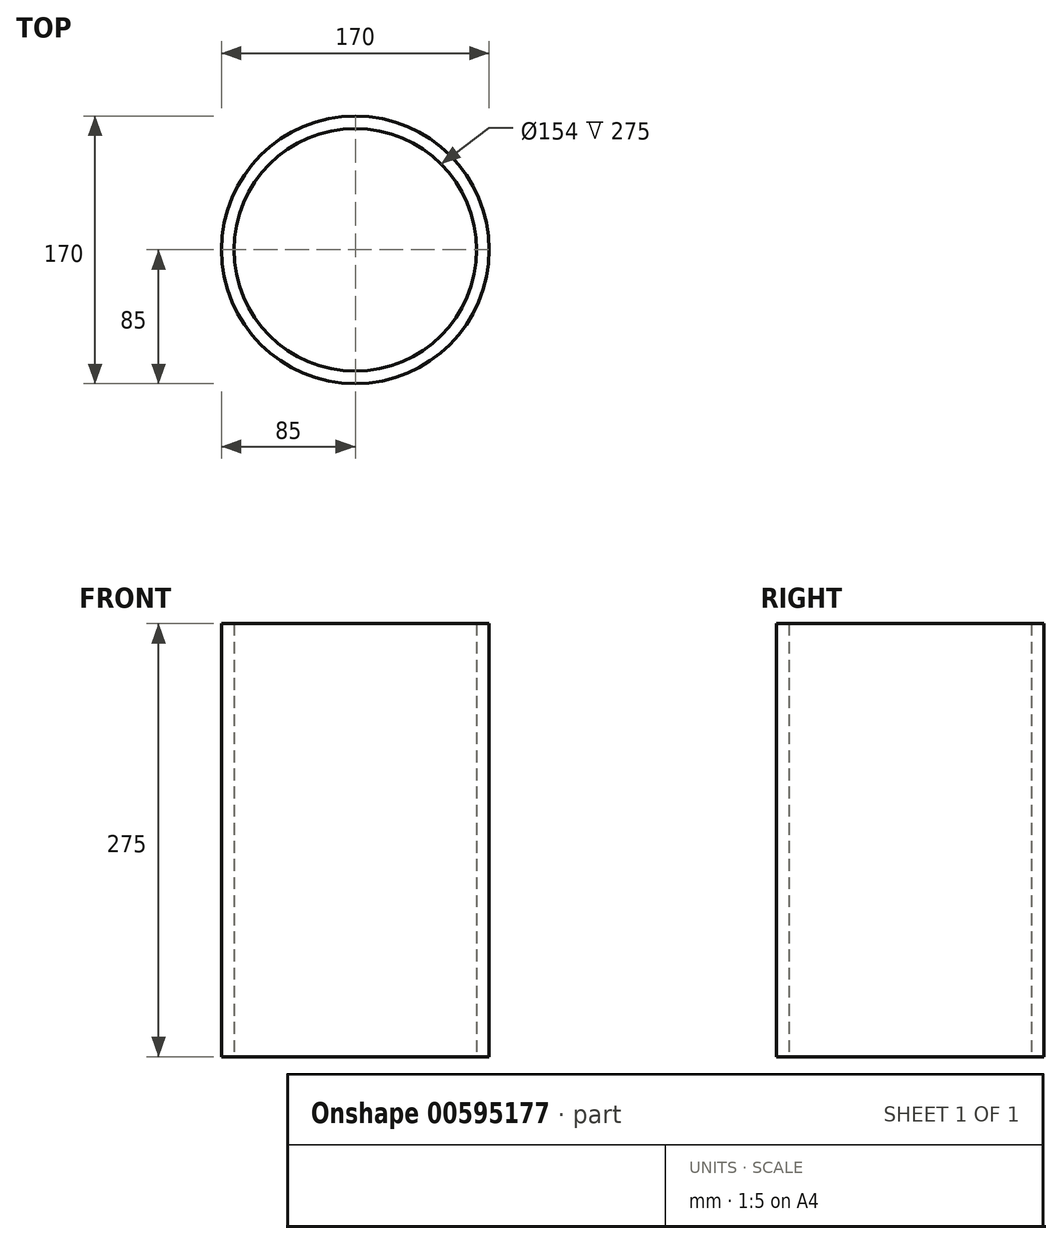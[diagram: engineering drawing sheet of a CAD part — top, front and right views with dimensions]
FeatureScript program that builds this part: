
annotation { "Feature Type Name" : "Feature", "Feature Type Description" : "" }
export const myFeature = defineFeature(function(context is Context, id is Id, definition is map)
    precondition{}
    {
        {
            var Q0;
            Q0=qCreatedBy(makeId("Top.planeOp"),FACE);
            var sketch = newSketch(context, id + "F0", { "sketchPlane" : qUnion([Q0])});
            skCircle(sketch, "E0", {"center": v(0, 0) * mm, "radius": 85 * mm});
            skCircle(sketch, "E1.0", {"center": v(0, 0) * mm, "radius": 77 * mm});
            skSolve(sketch);
        }
        {
            var Q0;
            Q0=makeQuery(id+"F0.imprint","IMPRINT",FACE,{"disambiguationData":[TD([[makeQuery(id+"F0.imprint","IMPRINT",EDGE,{"derivedFrom":sQuery(id+"F0.wireOp",EDGE,"E0")}),1.0]])]});
            extrude(context, id + "F1", {"entities" : qUnion([Q0]), "depth" : 315 * mm, "offsetDistance" : 25 * mm});
        }
        {
            var Q0;
            Q0=qCreatedBy(makeId("Front.planeOp"),FACE);
            cPlane(context, id + "F2", {"entities" : qUnion([Q0]), "cplaneType" : CPlaneType.OFFSET, "offset" : 85 * mm, "oppositeDirection" : true, "width" : 150 * mm, "height" : 150 * mm});
        }
        {
            var Q0;
            Q0=makeQuery(id+"F1.opExtrude","CAP_FACE",FACE,{"disambiguationData":[OSD([sQuery(id+"F0.wireOp",EDGE,"E0"),sQuery(id+"F0.wireOp",EDGE,"E1.0")])],"isStart":false});
            var sketch = newSketch(context, id + "F3", { "sketchPlane" : qUnion([Q0])});
            skCircle(sketch, "E2", {"center": v(0, 0) * mm, "radius": 90 * mm});
            skSolve(sketch);
        }
        {
            var Q0;
            Q0=makeQuery(id+"F3.imprint","IMPRINT",FACE,{"disambiguationData":[TD([[makeQuery(id+"F3.imprint","IMPRINT",EDGE,{"derivedFrom":makeQuery(id+"F1.opExtrude","CAP_EDGE",EDGE,{"disambiguationData":[OSD([sQuery(id+"F0.wireOp",EDGE,"E1.0")])],"isStart":false})}),1.0]])]});
            var Q1;
            Q1=makeQuery(id+"F3.imprint","IMPRINT",FACE,{"disambiguationData":[TD([[makeQuery(id+"F3.imprint","IMPRINT",EDGE,{"derivedFrom":makeQuery(id+"F1.opExtrude","CAP_EDGE",EDGE,{"disambiguationData":[OSD([sQuery(id+"F0.wireOp",EDGE,"E0")])],"isStart":false})}),1.0]])]});
            extrude(context, id + "F4", {"entities" : qUnion([Q0, Q1]), "operationType" : NewBodyOperationType.REMOVE, "oppositeDirection" : true, "depth" : 40 * mm, "offsetDistance" : 25 * mm});
        }
    });
